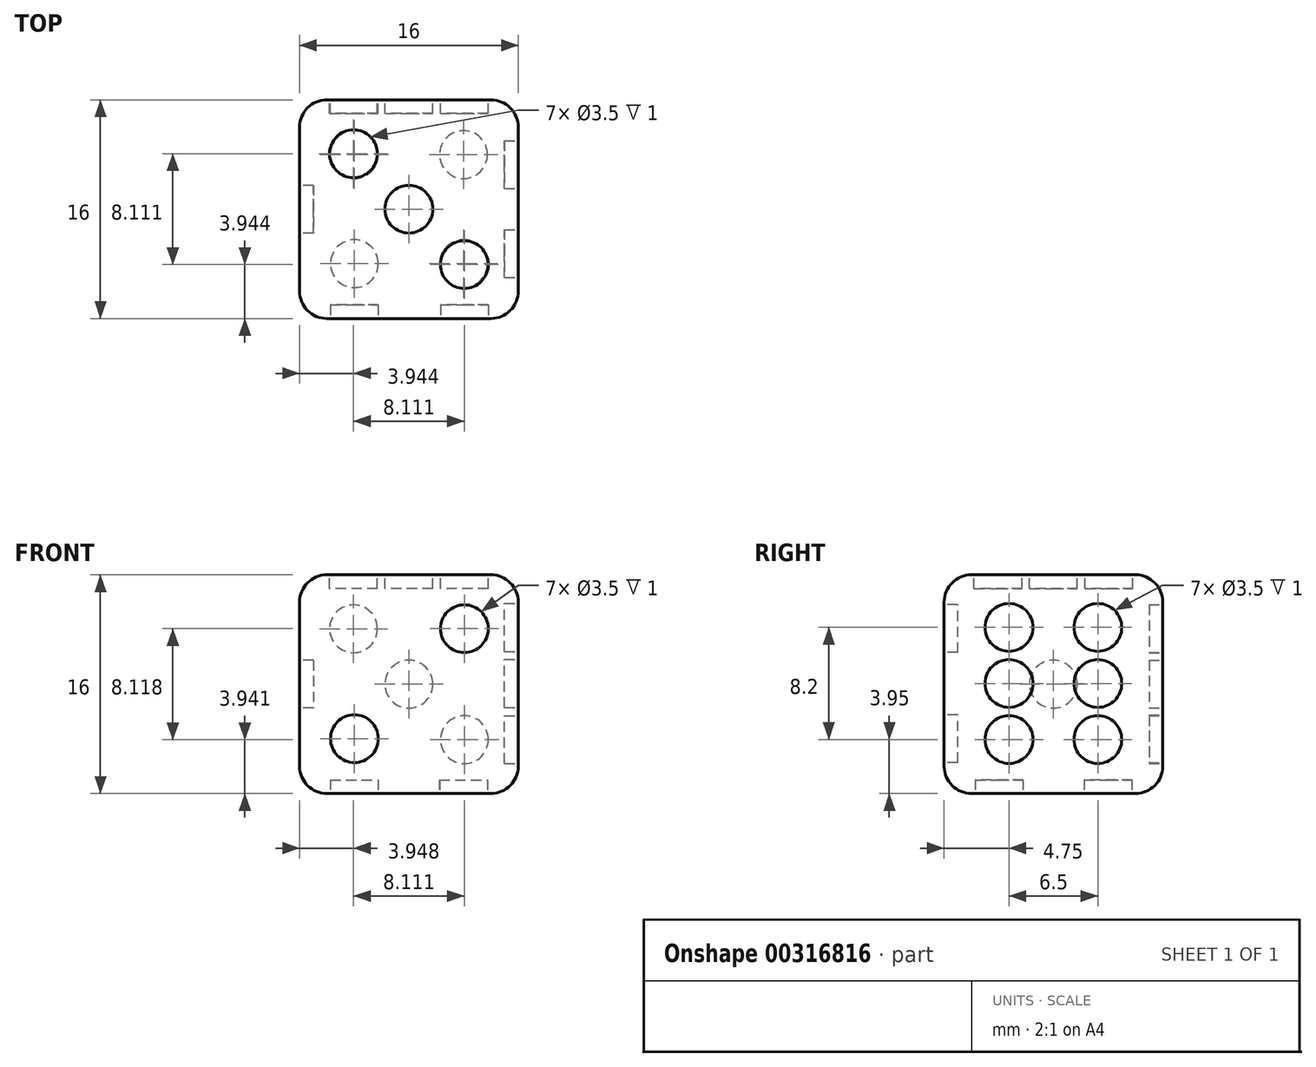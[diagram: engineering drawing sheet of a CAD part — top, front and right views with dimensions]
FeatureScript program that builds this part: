
annotation { "Feature Type Name" : "Feature", "Feature Type Description" : "" }
export const myFeature = defineFeature(function(context is Context, id is Id, definition is map)
    precondition{}
    {
        {
            var Q0;
            Q0=qCreatedBy(makeId("Right.planeOp"),FACE);
            var sketch = newSketch(context, id + "F0", { "sketchPlane" : qUnion([Q0])});
            skLineSegment(sketch, "E0.bottom", {"start": v(8, -8) * mm, "end": v(-8, -8) * mm});
            skLineSegment(sketch, "E0.top", {"start": v(8, 8) * mm, "end": v(-8, 8) * mm});
            skLineSegment(sketch, "E0.left", {"start": v(8, -8) * mm, "end": v(8, 8) * mm});
            skLineSegment(sketch, "E0.right", {"start": v(-8, -8) * mm, "end": v(-8, 8) * mm});
            skPoint(sketch, "E0.middle", {"position": v(0, 0) * mm});
            skSolve(sketch);
        }
        {
            var Q0;
            Q0 = qSketchRegion(id + "F0", true);
            extrude(context, id + "F1", {"entities" : qUnion([Q0]), "endBound" : BoundingType.SYMMETRIC, "depth" : 16 * mm});
        }
        {
            var Q0;
            Q0=makeQuery(id+"F1.opExtrude","CAP_EDGE",EDGE,{"disambiguationData":[OSD([sQuery(id+"F0.wireOp",EDGE,"E0.top")])],"isStart":false});
            var Q1;
            Q1=makeQuery(id+"F1.opExtrude","SWEPT_EDGE",EDGE,{"disambiguationData":[OSD([sQuery(id+"F0.wireOp",EDGE,"E0.top"),sQuery(id+"F0.wireOp",EDGE,"E0.right")])]});
            var Q2;
            Q2=makeQuery(id+"F1.opExtrude","CAP_EDGE",EDGE,{"disambiguationData":[OSD([sQuery(id+"F0.wireOp",EDGE,"E0.top")])],"isStart":true});
            var Q3;
            Q3=makeQuery(id+"F1.opExtrude","SWEPT_EDGE",EDGE,{"disambiguationData":[OSD([sQuery(id+"F0.wireOp",EDGE,"E0.top"),sQuery(id+"F0.wireOp",EDGE,"E0.left")])]});
            var Q4;
            Q4=makeQuery(id+"F1.opExtrude","CAP_EDGE",EDGE,{"disambiguationData":[OSD([sQuery(id+"F0.wireOp",EDGE,"E0.left")])],"isStart":true});
            var Q5;
            Q5=makeQuery(id+"F1.opExtrude","CAP_EDGE",EDGE,{"disambiguationData":[OSD([sQuery(id+"F0.wireOp",EDGE,"E0.bottom")])],"isStart":true});
            var Q6;
            Q6=makeQuery(id+"F1.opExtrude","CAP_EDGE",EDGE,{"disambiguationData":[OSD([sQuery(id+"F0.wireOp",EDGE,"E0.right")])],"isStart":true});
            var Q7;
            Q7=makeQuery(id+"F1.opExtrude","SWEPT_EDGE",EDGE,{"disambiguationData":[OSD([sQuery(id+"F0.wireOp",EDGE,"E0.bottom"),sQuery(id+"F0.wireOp",EDGE,"E0.left")])]});
            var Q8;
            Q8=makeQuery(id+"F1.opExtrude","SWEPT_EDGE",EDGE,{"disambiguationData":[OSD([sQuery(id+"F0.wireOp",EDGE,"E0.bottom"),sQuery(id+"F0.wireOp",EDGE,"E0.right")])]});
            var Q9;
            Q9=makeQuery(id+"F1.opExtrude","CAP_EDGE",EDGE,{"disambiguationData":[OSD([sQuery(id+"F0.wireOp",EDGE,"E0.bottom")])],"isStart":false});
            var Q10;
            Q10=makeQuery(id+"F1.opExtrude","CAP_EDGE",EDGE,{"disambiguationData":[OSD([sQuery(id+"F0.wireOp",EDGE,"E0.left")])],"isStart":false});
            var Q11;
            Q11=makeQuery(id+"F1.opExtrude","CAP_EDGE",EDGE,{"disambiguationData":[OSD([sQuery(id+"F0.wireOp",EDGE,"E0.right")])],"isStart":false});
            fillet(context, id + "F2", {"entities" : qUnion([Q0, Q1, Q2, Q3, Q4, Q5, Q6, Q7, Q8, Q9, Q10, Q11]), "radius" : 2 * mm, "tangentPropagation" : true, "allowEdgeOverflow" : false});
        }
        {
            var Q0;
            Q0=makeQuery(id+"F1.opExtrude","CAP_FACE",FACE,{"disambiguationData":[OSD([sQuery(id+"F0.wireOp",EDGE,"E0.bottom"),sQuery(id+"F0.wireOp",EDGE,"E0.top"),sQuery(id+"F0.wireOp",EDGE,"E0.left"),sQuery(id+"F0.wireOp",EDGE,"E0.right")])],"isStart":false});
            var sketch = newSketch(context, id + "F3", { "sketchPlane" : qUnion([Q0])});
            skCircle(sketch, "E1", {"center": v(-3.25, 4.15) * mm, "radius": 1.75 * mm});
            skCircle(sketch, "E2", {"center": v(-3.25, 0.05) * mm, "radius": 1.75 * mm});
            skCircle(sketch, "E3", {"center": v(-3.25, -4.05) * mm, "radius": 1.75 * mm});
            skCircle(sketch, "E4", {"center": v(3.25, 4.15) * mm, "radius": 1.75 * mm});
            skCircle(sketch, "E5", {"center": v(3.25, 0.05) * mm, "radius": 1.75 * mm});
            skCircle(sketch, "E6", {"center": v(3.25, -4.05) * mm, "radius": 1.75 * mm});
            skSolve(sketch);
        }
        {
            var Q0;
            Q0=makeQuery(id+"F3.imprint","IMPRINT",FACE,{"disambiguationData":[TD([[makeQuery(id+"F3.imprint","IMPRINT",EDGE,{"derivedFrom":sQuery(id+"F3.wireOp",EDGE,"E1")}),1.0]])]});
            var Q1;
            Q1=makeQuery(id+"F3.imprint","IMPRINT",FACE,{"disambiguationData":[TD([[makeQuery(id+"F3.imprint","IMPRINT",EDGE,{"derivedFrom":sQuery(id+"F3.wireOp",EDGE,"E2")}),1.0]])]});
            var Q2;
            Q2=makeQuery(id+"F3.imprint","IMPRINT",FACE,{"disambiguationData":[TD([[makeQuery(id+"F3.imprint","IMPRINT",EDGE,{"derivedFrom":sQuery(id+"F3.wireOp",EDGE,"E3")}),1.0]])]});
            var Q3;
            Q3=makeQuery(id+"F3.imprint","IMPRINT",FACE,{"disambiguationData":[TD([[makeQuery(id+"F3.imprint","IMPRINT",EDGE,{"derivedFrom":sQuery(id+"F3.wireOp",EDGE,"E6")}),1.0]])]});
            var Q4;
            Q4=makeQuery(id+"F3.imprint","IMPRINT",FACE,{"disambiguationData":[TD([[makeQuery(id+"F3.imprint","IMPRINT",EDGE,{"derivedFrom":sQuery(id+"F3.wireOp",EDGE,"E5")}),1.0]])]});
            var Q5;
            Q5=makeQuery(id+"F3.imprint","IMPRINT",FACE,{"disambiguationData":[TD([[makeQuery(id+"F3.imprint","IMPRINT",EDGE,{"derivedFrom":sQuery(id+"F3.wireOp",EDGE,"E4")}),1.0]])]});
            extrude(context, id + "F4", {"entities" : qUnion([Q0, Q1, Q2, Q3, Q4, Q5]), "operationType" : NewBodyOperationType.REMOVE, "oppositeDirection" : true, "depth" : 1 * mm});
        }
        {
            var Q0;
            Q0=makeQuery(id+"F1.opExtrude","SWEPT_FACE",FACE,{"disambiguationData":[OSD([sQuery(id+"F0.wireOp",EDGE,"E0.top")])]});
            var sketch = newSketch(context, id + "F5", { "sketchPlane" : qUnion([Q0])});
            skCircle(sketch, "E7", {"center": v(0, 0) * mm, "radius": 1.75 * mm});
            skCircle(sketch, "E8", {"center": v(-4.06, 4.06) * mm, "radius": 1.75 * mm});
            skCircle(sketch, "E9", {"center": v(4.06, -4.06) * mm, "radius": 1.75 * mm});
            skSolve(sketch);
        }
        {
            var Q0;
            Q0 = qSketchRegion(id + "F5", true);
            extrude(context, id + "F6", {"entities" : qUnion([Q0]), "operationType" : NewBodyOperationType.REMOVE, "oppositeDirection" : true, "depth" : 1 * mm});
        }
        {
            var Q0;
            Q0=makeQuery(id+"F1.opExtrude","SWEPT_FACE",FACE,{"disambiguationData":[OSD([sQuery(id+"F0.wireOp",EDGE,"E0.left")])]});
            var sketch = newSketch(context, id + "F7", { "sketchPlane" : qUnion([Q0])});
            skCircle(sketch, "E10", {"center": v(0, 0) * mm, "radius": 1.75 * mm});
            skCircle(sketch, "E11", {"center": v(-4.06, 4.06) * mm, "radius": 1.75 * mm});
            skCircle(sketch, "E12", {"center": v(3.99, -3.99) * mm, "radius": 1.75 * mm});
            skCircle(sketch, "E13", {"center": v(4.05, 4.05) * mm, "radius": 1.75 * mm});
            skCircle(sketch, "E14", {"center": v(-4.06, -4.06) * mm, "radius": 1.75 * mm});
            skSolve(sketch);
        }
        {
            var Q0;
            Q0 = qSketchRegion(id + "F7", true);
            extrude(context, id + "F8", {"entities" : qUnion([Q0]), "operationType" : NewBodyOperationType.REMOVE, "oppositeDirection" : true, "depth" : 1 * mm});
        }
        {
            var Q0;
            Q0=makeQuery(id+"F1.opExtrude","CAP_FACE",FACE,{"disambiguationData":[OSD([sQuery(id+"F0.wireOp",EDGE,"E0.bottom"),sQuery(id+"F0.wireOp",EDGE,"E0.top"),sQuery(id+"F0.wireOp",EDGE,"E0.left"),sQuery(id+"F0.wireOp",EDGE,"E0.right")])],"isStart":true});
            var sketch = newSketch(context, id + "F9", { "sketchPlane" : qUnion([Q0])});
            skCircle(sketch, "E15", {"center": v(0, 0) * mm, "radius": 1.75 * mm});
            skSolve(sketch);
        }
        {
            var Q0;
            Q0 = qSketchRegion(id + "F9", true);
            extrude(context, id + "F10", {"entities" : qUnion([Q0]), "operationType" : NewBodyOperationType.REMOVE, "oppositeDirection" : true, "depth" : 1 * mm});
        }
        {
            var Q0;
            Q0=makeQuery(id+"F1.opExtrude","SWEPT_FACE",FACE,{"disambiguationData":[OSD([sQuery(id+"F0.wireOp",EDGE,"E0.bottom")])]});
            var sketch = newSketch(context, id + "F11", { "sketchPlane" : qUnion([Q0])});
            skCircle(sketch, "E16", {"center": v(-3.99, 3.99) * mm, "radius": 1.75 * mm});
            skCircle(sketch, "E17", {"center": v(-4, -4) * mm, "radius": 1.75 * mm});
            skCircle(sketch, "E18", {"center": v(3.99, 3.99) * mm, "radius": 1.75 * mm});
            skCircle(sketch, "E19", {"center": v(4, -4) * mm, "radius": 1.75 * mm});
            skSolve(sketch);
        }
        {
            var Q0;
            Q0 = qSketchRegion(id + "F11", true);
            extrude(context, id + "F12", {"entities" : qUnion([Q0]), "operationType" : NewBodyOperationType.REMOVE, "oppositeDirection" : true, "depth" : 1 * mm});
        }
        {
            var Q0;
            Q0=makeQuery(id+"F1.opExtrude","SWEPT_FACE",FACE,{"disambiguationData":[OSD([sQuery(id+"F0.wireOp",EDGE,"E0.right")])]});
            var sketch = newSketch(context, id + "F13", { "sketchPlane" : qUnion([Q0])});
            skCircle(sketch, "E20", {"center": v(4.06, 4.06) * mm, "radius": 1.75 * mm});
            skCircle(sketch, "E21", {"center": v(-3.99, -3.99) * mm, "radius": 1.75 * mm});
            skSolve(sketch);
        }
        {
            var Q0;
            Q0 = qSketchRegion(id + "F13", true);
            extrude(context, id + "F14", {"entities" : qUnion([Q0]), "operationType" : NewBodyOperationType.REMOVE, "oppositeDirection" : true, "depth" : 1 * mm});
        }
    });
